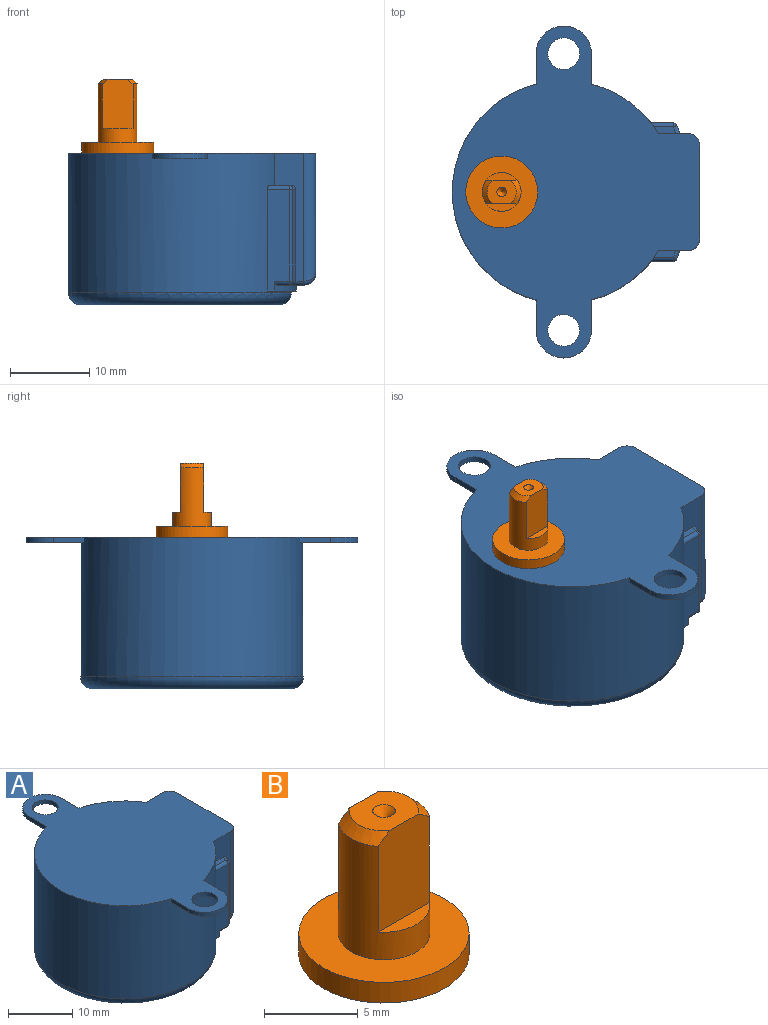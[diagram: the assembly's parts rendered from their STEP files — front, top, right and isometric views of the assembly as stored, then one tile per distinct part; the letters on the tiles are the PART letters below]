
ASSEMBLY  parts=2 mates=1
PART A: 56 faces, bbox 32.5x42x19.2 mm
  f0: plane 15.2x11.8mm, normal (1,0,0), area 169.8mm2, adj f14,f29,f30,f31,f51,f52,f53,f54
  f1: cylinder r=14.1mm len=28.2mm, axis (0,0,1), area 1244mm2, adj f2,f3,f4,f5,f6,f7,f8,f13
  f2: plane 16.5x3.36mm, normal (0,0,-1), area 25.3mm2, adj f1,f23,f24,f26,f27,f30,f37,f39
  f3: plane 16.2x3.7mm, normal (0,1,0), area 27.3mm2, adj f1,f14,f17,f18,f29,f33,f40
  f4: plane 3.84x0.75mm, normal (-1,0,0), area 2.9mm2, adj f1,f10,f13,f14
  f5: plane 3.84x0.75mm, normal (-1,0,0), area 2.9mm2, adj f1,f8,f9,f14
  f6: plane 3.84x0.75mm, normal (1,0,0), area 2.9mm2, adj f1,f10,f13,f14
  f7: plane 3.84x0.75mm, normal (1,0,0), area 2.9mm2, adj f1,f8,f9,f14
  f8: plane 7.34x7mm, normal (0,0,-1), area 31.5mm2, adj f1,f5,f7,f9,f12
  f9: cylinder r=3.5mm len=7mm, axis (0,0,1), area 8.2mm2, adj f5,f7,f8,f14
  f10: cylinder r=3.5mm len=7mm, axis (0,0,1), area 8.2mm2, adj f4,f6,f13,f14
  f11: cylinder r=2mm len=4mm, axis (0,0,1), area 9.4mm2, adj f13,f14
  f12: cylinder r=2mm len=4mm, axis (0,0,1), area 9.4mm2, adj f8,f14
  f13: plane 7.34x7mm, normal (0,0,-1), area 31.5mm2, adj f1,f4,f6,f10,f11
  f14: plane 42x31.3mm, normal (0,0,1), area 742.5mm2, adj f0,f1,f3,f4,f5,f6,f7,f9
  f15: plane 25.2x25.2mm, normal (0,0,-1), area 498.8mm2, adj f32
  f16: plane 16.2x3.7mm, normal (0,-1,0), area 27.3mm2, adj f1,f14,f20,f21,f31,f43,f49
  f17: plane 2.73x0.85mm, normal (0,0,1), area 1.9mm2, adj f1,f3,f33,f34
  f18: plane 11.6x1.02mm, normal (0.94,0.35,0), area 12.7mm2, adj f3,f33,f36,f39
  f19: plane 12.85x2.8mm, normal (0,1,0), area 33.6mm2, adj f1,f24,f25,f34,f36,f37
  f20: plane 2.73x0.85mm, normal (0,0,1), area 1.9mm2, adj f1,f16,f42,f43
  f21: plane 11.6x1.02mm, normal (0.94,-0.35,0), area 12.7mm2, adj f16,f43,f46,f48
  f22: plane 12.85x2.8mm, normal (0,-1,0), area 33.6mm2, adj f1,f26,f28,f42,f45,f46
  f23: plane 0.75x0.75mm, normal (0,-1,0), area 0.6mm2, adj f1,f2,f24,f25
  f24: cylinder r=14.85mm len=7.25mm, axis (0,0,1), area 6mm2, adj f2,f19,f23,f25,f37
  f25: plane 7.25x3.71mm, normal (0,0,-1), area 5.9mm2, adj f1,f19,f23,f24
  f26: cylinder r=14.85mm len=7.25mm, axis (0,0,1), area 6mm2, adj f2,f22,f27,f28,f45
  f27: plane 0.75x0.75mm, normal (0,1,0), area 0.6mm2, adj f1,f2,f26,f28
  f28: plane 7.25x3.71mm, normal (0,0,-1), area 5.9mm2, adj f1,f22,f26,f27
  f29: cylinder r=1.5mm len=16.2mm, axis (0,0,-1), area 37.3mm2, adj f0,f3,f14,f41
  f30: cylinder r=1.5mm len=13.8mm, axis (0,-1,0), area 30.8mm2, adj f0,f2,f41,f50
  f31: cylinder r=1.5mm len=16.2mm, axis (0,0,1), area 37.3mm2, adj f0,f14,f16,f50
  f32: torus R=12.6mm, axis (0,0,-1), area 200.7mm2, adj f1,f15
  f33: cylinder r=0.5mm len=1.2mm, axis (-0.35,0.94,0), area 0.8mm2, adj f3,f17,f18,f35
  f34: cylinder r=0.5mm len=2.8mm, axis (-1,0,0), area 2.1mm2, adj f1,f17,f19,f35
  f35: sphere r=0.5mm, area 0.3mm2, adj f33,f34,f36
  f36: cylinder r=0.5mm len=11.6mm, axis (0,0,-1), area 7.1mm2, adj f18,f19,f35,f38
  f37: cylinder r=0.5mm len=1.86mm, axis (-1,0,0), area 1.4mm2, adj f2,f19,f24,f38
  f38: sphere r=0.5mm, area 0.3mm2, adj f36,f37,f39
  f39: cylinder r=0.5mm len=1.52mm, axis (-0.35,0.94,0), area 1mm2, adj f2,f18,f38,f40
  f40: cylinder r=0.5mm len=1.35mm, axis (1,0,0), area 0.9mm2, adj f2,f3,f39,f41
  f41: bspline ~1.76x1.5mm, area 1.3mm2, adj f29,f30,f40
  f42: cylinder r=0.5mm len=2.8mm, axis (1,0,0), area 2.1mm2, adj f1,f20,f22,f44
  f43: cylinder r=0.5mm len=1.2mm, axis (0.35,0.94,0), area 0.8mm2, adj f16,f20,f21,f44
  f44: sphere r=0.5mm, area 0.3mm2, adj f42,f43,f46
  f45: cylinder r=0.5mm len=1.86mm, axis (1,0,0), area 1.4mm2, adj f2,f22,f26,f47
  f46: cylinder r=0.5mm len=11.6mm, axis (0,0,-1), area 7.1mm2, adj f21,f22,f44,f47
  f47: sphere r=0.5mm, area 0.3mm2, adj f45,f46,f48
  f48: cylinder r=0.5mm len=1.52mm, axis (0.35,0.94,0), area 1mm2, adj f2,f21,f47,f49
  f49: cylinder r=0.5mm len=1.35mm, axis (-1,0,0), area 0.9mm2, adj f2,f16,f48,f50
  f50: bspline ~1.76x1.5mm, area 1.3mm2, adj f30,f31,f49
  f51: plane 6.3x1mm, normal (0,0,1), area 6.3mm2, adj f0,f52,f54,f55
  f52: cylinder r=0.65mm len=1.3mm, axis (1,0,0), area 2mm2, adj f0,f51,f53,f55
  f53: plane 6.3x1mm, normal (0,0,-1), area 6.3mm2, adj f0,f52,f54,f55
  f54: cylinder r=0.65mm len=1.3mm, axis (1,0,0), area 2mm2, adj f0,f51,f53,f55
  f55: plane 7.6x1.3mm, normal (1,0,0), area 9.5mm2, adj f51,f52,f53,f54
PART B: 12 faces, bbox 9.2x9.2x9.5 mm
  f0: cylinder r=2.45mm len=7.4mm, axis (0,0,-1), area 63.9mm2, adj f1,f2,f4,f8,f9,f10,f11
  f1: cone r=1.85mm half-angle=45deg, axis (0,0,-1), area 2.9mm2, adj f0,f3,f9,f11
  f2: cone r=1.85mm half-angle=45deg, axis (0,0,-1), area 2.9mm2, adj f0,f3,f9,f11
  f3: plane 3.7x3mm, normal (0,0,1), area 8.6mm2, adj f1,f2,f5,f9,f11
  f4: plane 9.1x9.1mm, normal (0,0,1), area 46.2mm2, adj f0,f7
  f5: cone r=0.6mm half-angle=45deg, axis (0,0,1), area 1.6mm2, adj f3
  f6: plane 9.1x9.1mm, normal (0,0,-1), area 65mm2, adj f7
  f7: cylinder r=4.55mm len=9.1mm, axis (0,0,-1), area 38.6mm2, adj f4,f6
  f8: plane 3.87x0.95mm, normal (0,0,1), area 2.6mm2, adj f0,f9
  f9: plane 6.31x3.98mm, normal (0,-1,0), area 23.5mm2, adj f0,f1,f2,f3,f8
  f10: plane 3.87x0.95mm, normal (0,0,1), area 2.6mm2, adj f0,f11
  f11: plane 6.31x3.98mm, normal (0,1,0), area 23.5mm2, adj f0,f1,f2,f3,f10
PLACE A t=(-8.98,0,0)mm
PLACE B t=(-8.98,0,0)mm
MATE fastened A.f1 <-> B.f6  axis (0,0,1) through (-1.13,0,0)mm
